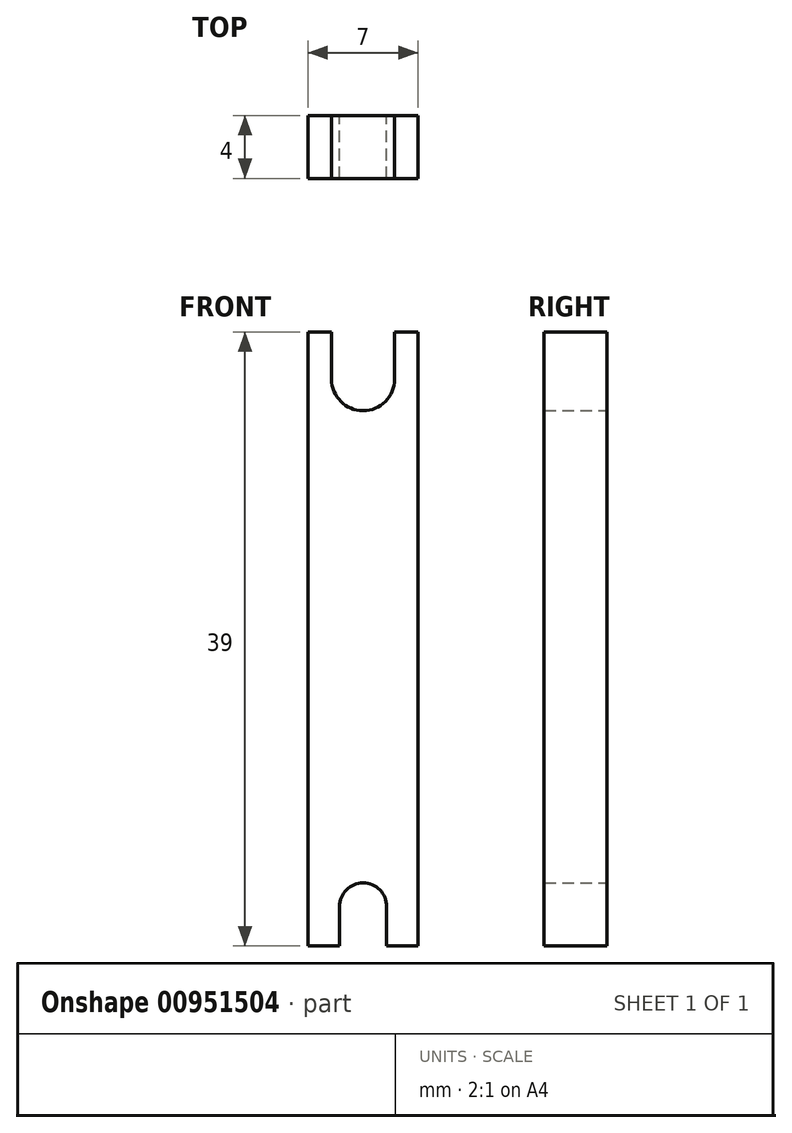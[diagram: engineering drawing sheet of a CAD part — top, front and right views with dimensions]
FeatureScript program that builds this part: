
annotation { "Feature Type Name" : "Feature", "Feature Type Description" : "" }
export const myFeature = defineFeature(function(context is Context, id is Id, definition is map)
    precondition{}
    {
        {
            var Q0;
            Q0=qCreatedBy(makeId("Front.planeOp"),FACE);
            var sketch = newSketch(context, id + "F0", { "sketchPlane" : qUnion([Q0])});
            skPoint(sketch, "E0.middle", {"position": v(0, 0) * mm});
            skCircle(sketch, "E1", {"center": v(0, 12) * mm, "radius": 2 * mm});
            skCircle(sketch, "E2", {"center": v(0, -21.5) * mm, "radius": 1.5 * mm});
            skLineSegment(sketch, "E3", {"start": v(-3.5, 0) * mm, "end": v(-3.5, 15) * mm});
            skLineSegment(sketch, "E4", {"start": v(-3.5, 15) * mm, "end": v(3.5, 15) * mm});
            skLineSegment(sketch, "E5", {"start": v(3.5, 15) * mm, "end": v(3.5, -24) * mm});
            skLineSegment(sketch, "E6", {"start": v(3.5, -24) * mm, "end": v(-3.5, -24) * mm});
            skLineSegment(sketch, "E7", {"start": v(-3.5, -24) * mm, "end": v(-3.5, 0) * mm});
            skLineSegment(sketch, "E8", {"start": v(-2, 15) * mm, "end": v(-2, 12) * mm});
            skLineSegment(sketch, "E9", {"start": v(2, 12) * mm, "end": v(2, 15) * mm});
            skLineSegment(sketch, "E10", {"start": v(1.5, -21.5) * mm, "end": v(1.5, -24) * mm});
            skLineSegment(sketch, "E11", {"start": v(-1.5, -21.5) * mm, "end": v(-1.5, -24) * mm});
            skSolve(sketch);
        }
        {
            var Q0;
            {var subQ10=sQuery(id+"F0.wireOp",EDGE,"E3");Q0=makeQuery(id+"F0.imprint","IMPRINT",FACE,{"disambiguationData":[TD([[makeQuery(id+"F0.imprint","IMPRINT",EDGE,{"derivedFrom":subQ10}),-1.0]])]});}
            extrude(context, id + "F1", {"entities" : qUnion([Q0]), "depth" : 4 * mm, "offsetDistance" : 25 * mm});
        }
    });
